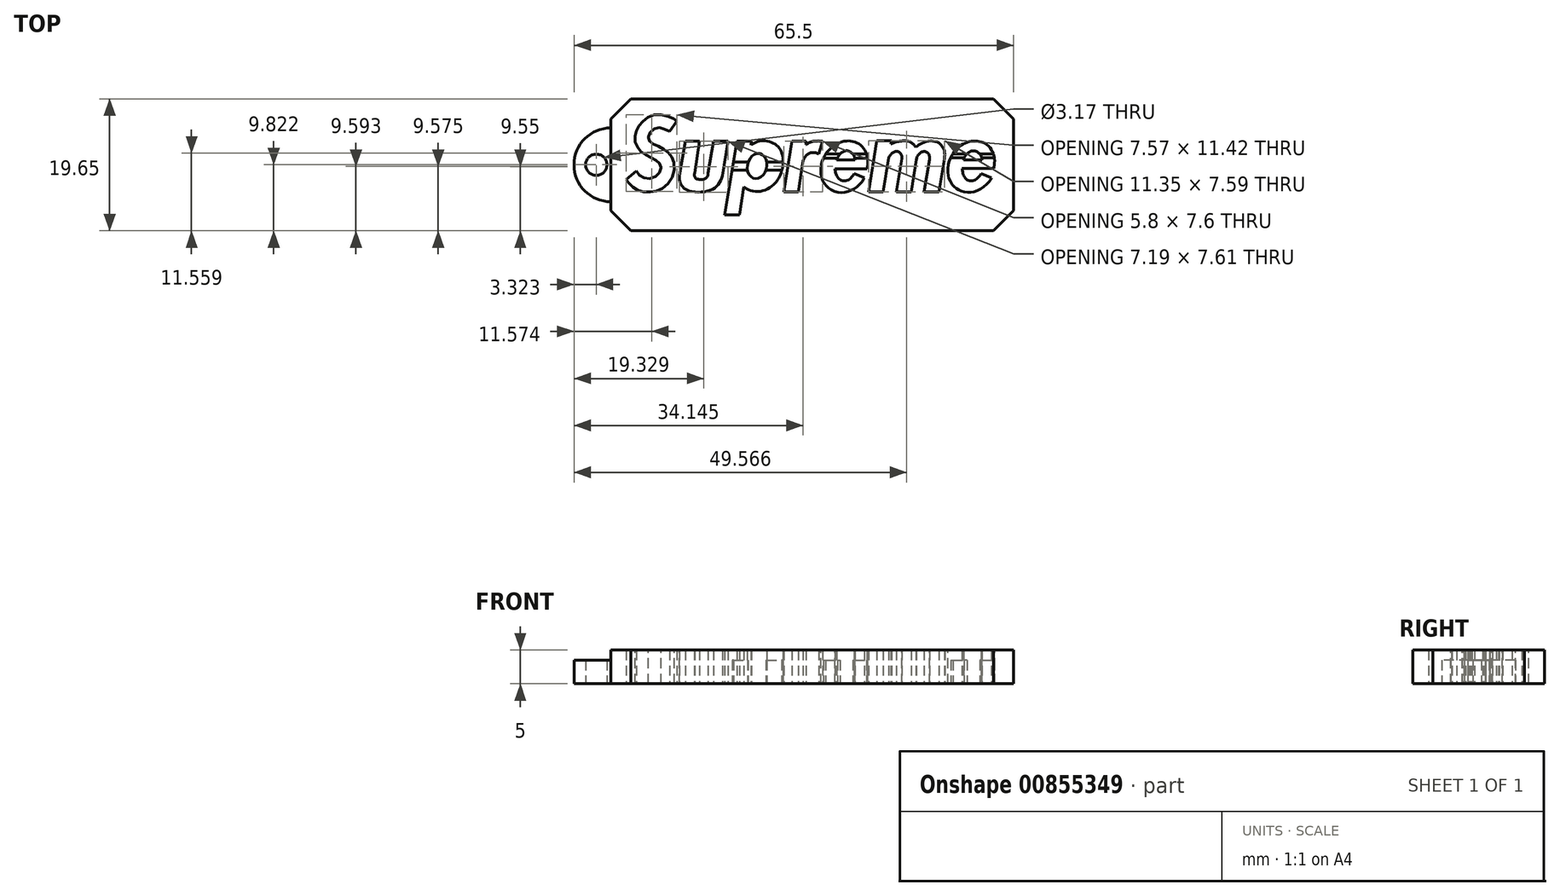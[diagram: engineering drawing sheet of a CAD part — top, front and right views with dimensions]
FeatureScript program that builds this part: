
annotation { "Feature Type Name" : "Feature", "Feature Type Description" : "" }
export const myFeature = defineFeature(function(context is Context, id is Id, definition is map)
    precondition{}
    {
        {
            var Q0;
            Q0=qCreatedBy(makeId("Top.planeOp"),FACE);
            var sketch = newSketch(context, id + "F0", { "sketchPlane" : qUnion([Q0])});
            skLineSegment(sketch, "E0", {"start": v(-20.13, 12.27) * mm, "end": v(-21.24, 10.76) * mm});
            skLineSegment(sketch, "E1", {"start": v(-26.2, 4.84) * mm, "end": v(-27.7, 3.62) * mm});
            skLineSegment(sketch, "E2", {"start": v(-18.91, 9.32) * mm, "end": v(-16.78, 9.32) * mm});
            skLineSegment(sketch, "E3", {"start": v(-18.91, 9.32) * mm, "end": v(-19.76, 4.22) * mm});
            skLineSegment(sketch, "E4", {"start": v(-12.57, 9.32) * mm, "end": v(-13.34, 4.17) * mm});
            skLineSegment(sketch, "E5", {"start": v(-16.78, 9.32) * mm, "end": v(-17.52, 4.58) * mm});
            skLineSegment(sketch, "E6", {"start": v(-14.7, 9.32) * mm, "end": v(-15.5, 4.52) * mm});
            skLineSegment(sketch, "E7", {"start": v(-11.2, 9.31) * mm, "end": v(-9.07, 9.31) * mm});
            skLineSegment(sketch, "E8", {"start": v(-9.07, 9.31) * mm, "end": v(-9.14, 8.73) * mm});
            skLineSegment(sketch, "E9", {"start": v(-11.2, 9.31) * mm, "end": v(-13.03, -1.66) * mm});
            skLineSegment(sketch, "E10", {"start": v(-13.03, -1.66) * mm, "end": v(-10.85, -1.66) * mm});
            skLineSegment(sketch, "E11", {"start": v(-10.85, -1.66) * mm, "end": v(-10.17, 2.52) * mm});
            skLineSegment(sketch, "E12", {"start": v(-3.04, 9.32) * mm, "end": v(-0.9, 9.32) * mm});
            skLineSegment(sketch, "E13", {"start": v(-0.9, 9.32) * mm, "end": v(-0.95, 8.78) * mm});
            skLineSegment(sketch, "E14", {"start": v(-3.04, 9.32) * mm, "end": v(-4.25, 1.75) * mm});
            skLineSegment(sketch, "E15", {"start": v(-4.25, 1.75) * mm, "end": v(-2.07, 1.75) * mm});
            skLineSegment(sketch, "E16", {"start": v(-2.07, 1.75) * mm, "end": v(-1.33, 6.4) * mm});
            skLineSegment(sketch, "E17", {"start": v(3.64, 6.52) * mm, "end": v(6.38, 6.52) * mm});
            skLineSegment(sketch, "E18", {"start": v(3.43, 5.2) * mm, "end": v(8.15, 5.2) * mm});
            skLineSegment(sketch, "E19", {"start": v(6.25, 4.47) * mm, "end": v(7.79, 3.88) * mm});
            skLineSegment(sketch, "E20", {"start": v(9.64, 9.35) * mm, "end": v(8.4, 1.77) * mm});
            skLineSegment(sketch, "E21", {"start": v(8.4, 1.77) * mm, "end": v(10.57, 1.77) * mm});
            skLineSegment(sketch, "E22", {"start": v(18.92, 1.77) * mm, "end": v(19.72, 6.72) * mm});
            skLineSegment(sketch, "E23", {"start": v(9.64, 9.35) * mm, "end": v(11.83, 9.35) * mm});
            skLineSegment(sketch, "E24", {"start": v(11.83, 9.35) * mm, "end": v(11.75, 8.85) * mm});
            skLineSegment(sketch, "E25", {"start": v(13.34, 6.69) * mm, "end": v(12.56, 1.77) * mm});
            skLineSegment(sketch, "E26", {"start": v(15.51, 6.6) * mm, "end": v(14.75, 1.77) * mm});
            skLineSegment(sketch, "E27", {"start": v(17.5, 6.6) * mm, "end": v(16.69, 1.77) * mm});
            skLineSegment(sketch, "E28", {"start": v(22.59, 6.5) * mm, "end": v(25.34, 6.5) * mm});
            skLineSegment(sketch, "E29", {"start": v(22.35, 5.22) * mm, "end": v(27.06, 5.22) * mm});
            skLineSegment(sketch, "E30", {"start": v(25.19, 4.5) * mm, "end": v(26.72, 3.88) * mm});
            skFitSpline(sketch, "E31", {"points": [v(-20.13, 12.27) * mm, v(-20.76, 12.7) * mm, v(-22.11, 13.2) * mm, v(-23.8, 13.15) * mm, v(-25.2, 12.27) * mm, v(-25.93, 11.36) * mm, v(-26.3, 10.37) * mm, v(-26.36, 9.25) * mm, v(-25.87, 8.18) * mm, v(-25.1, 7.42) * mm, v(-23.81, 6.77) * mm, v(-23.11, 6.36) * mm, v(-22.57, 5.74) * mm, v(-22.67, 4.82) * mm, v(-23.38, 4) * mm, v(-24.59, 3.73) * mm, v(-25.6, 4.14) * mm, v(-26.2, 4.84) * mm], "startDerivative": vector(-11.62, 8.81) * mm, "endDerivative": vector(-10.29, 14.16) * mm});
            skFitSpline(sketch, "E32", {"points": [v(-27.7, 3.62) * mm, v(-27.33, 3.07) * mm, v(-26.53, 2.34) * mm, v(-25.49, 1.83) * mm, v(-24.08, 1.73) * mm, v(-22.83, 2) * mm, v(-21.52, 2.96) * mm, v(-20.6, 4.68) * mm, v(-20.7, 6.46) * mm, v(-21.18, 7.32) * mm, v(-21.96, 8.03) * mm, v(-22.95, 8.56) * mm, v(-23.88, 9) * mm, v(-24.3, 9.42) * mm, v(-24.39, 10.06) * mm, v(-23.98, 10.79) * mm, v(-23.08, 11.3) * mm, v(-22.14, 11.16) * mm, v(-21.24, 10.76) * mm], "startDerivative": vector(7.43, -12.37) * mm, "endDerivative": vector(16.77, -8.2) * mm});
            skFitSpline(sketch, "E33", {"points": [v(-19.76, 4.22) * mm, v(-19.76, 3.4) * mm, v(-19.1, 2.3) * mm, v(-17.7, 1.77) * mm, v(-15.88, 1.8) * mm, v(-14.59, 2.32) * mm, v(-13.86, 3.06) * mm, v(-13.34, 4.17) * mm], "startDerivative": vector(-0.86, -6.8) * mm, "endDerivative": vector(3.3, 8.4) * mm});
            skFitSpline(sketch, "E34", {"points": [v(-17.52, 4.58) * mm, v(-17.52, 4.17) * mm, v(-17.35, 3.77) * mm, v(-16.92, 3.62) * mm, v(-16.36, 3.59) * mm, v(-15.88, 3.77) * mm, v(-15.6, 4.1) * mm, v(-15.5, 4.52) * mm], "startDerivative": vector(-0.2, -2.97) * mm, "endDerivative": vector(0.35, 3.22) * mm});
            skLineSegment(sketch, "E35.trimOffspring", {"start": v(-14.7, 9.32) * mm, "end": v(-12.57, 9.32) * mm});
            skEllipse(sketch, "E36", {"center": v(-8.2, 5.6) * mm, "majorRadius": 1.9 * mm, "minorRadius": 1.44 * mm, "majorAxis": v(0.22, 0.98)});
            skFitSpline(sketch, "E37", {"points": [v(-9.14, 8.73) * mm, v(-8.13, 9.26) * mm, v(-6.71, 9.35) * mm, v(-5.34, 8.73) * mm, v(-4.62, 7.79) * mm, v(-4.33, 6.2) * mm, v(-4.76, 4.2) * mm, v(-5.68, 2.9) * mm, v(-7.67, 1.85) * mm, v(-9.7, 2.16) * mm, v(-10.17, 2.52) * mm], "startDerivative": vector(10.84, 6.9) * mm, "endDerivative": vector(-5.7, 5.72) * mm});
            skFitSpline(sketch, "E38", {"points": [v(-0.95, 8.78) * mm, v(0, 9.26) * mm, v(1.56, 9.33) * mm], "startDerivative": vector(1.92, 1.26) * mm, "endDerivative": vector(3.05, -0.12) * mm});
            skLineSegment(sketch, "E39", {"start": v(1.56, 9.33) * mm, "end": v(1, 7.4) * mm});
            skFitSpline(sketch, "E40", {"points": [v(-1.33, 6.4) * mm, v(-0.82, 7.24) * mm, v(0.11, 7.62) * mm, v(1, 7.4) * mm], "startDerivative": vector(1.2, 2.73) * mm, "endDerivative": vector(2.66, -1.05) * mm});
            skFitSpline(sketch, "E41", {"points": [v(3.64, 6.52) * mm, v(4.18, 7.4) * mm, v(5.24, 7.89) * mm, v(6.2, 7.19) * mm, v(6.38, 6.52) * mm], "startDerivative": vector(1.66, 3.64) * mm, "endDerivative": vector(0.33, -3.12) * mm});
            skFitSpline(sketch, "E42", {"points": [v(8.15, 5.2) * mm, v(8.3, 6.03) * mm, v(8.15, 7.13) * mm, v(7.79, 8.05) * mm, v(7.07, 8.82) * mm, v(6.2, 9.24) * mm, v(5.15, 9.34) * mm, v(3.86, 9) * mm, v(2.92, 8.39) * mm, v(2.2, 7.65) * mm, v(1.7, 6.8) * mm, v(1.35, 5.7) * mm, v(1.3, 4.54) * mm, v(1.58, 3.4) * mm, v(2.25, 2.5) * mm, v(3.17, 1.9) * mm, v(4.5, 1.65) * mm, v(5.69, 1.94) * mm, v(6.76, 2.58) * mm, v(7.6, 3.52) * mm, v(7.79, 3.88) * mm], "startDerivative": vector(4.46, 17.79) * mm, "endDerivative": vector(4.42, 10.4) * mm});
            skFitSpline(sketch, "E43", {"points": [v(6.25, 4.47) * mm, v(6.02, 4.1) * mm, v(5.38, 3.54) * mm, v(4.5, 3.4) * mm, v(3.85, 3.88) * mm, v(3.48, 4.6) * mm, v(3.43, 5.2) * mm], "startDerivative": vector(-1.48, -2.67) * mm, "endDerivative": vector(0, 3.83) * mm});
            skFitSpline(sketch, "E44", {"points": [v(11.41, 6.83) * mm, v(11.8, 7.4) * mm, v(12.42, 7.79) * mm, v(13.06, 7.59) * mm, v(13.37, 7.08) * mm, v(13.34, 6.69) * mm], "startDerivative": vector(1.57, 2.8) * mm, "endDerivative": vector(-0.51, -2.35) * mm});
            skFitSpline(sketch, "E45", {"points": [v(15.51, 6.6) * mm, v(15.78, 7.22) * mm, v(16.28, 7.67) * mm, v(16.79, 7.78) * mm, v(17.24, 7.54) * mm, v(17.47, 7.06) * mm, v(17.5, 6.6) * mm], "startDerivative": vector(1.16, 3.5) * mm, "endDerivative": vector(-0.05, -3) * mm});
            skFitSpline(sketch, "E46", {"points": [v(11.75, 8.85) * mm, v(12.3, 9.13) * mm, v(13.4, 9.35) * mm, v(14.5, 9.23) * mm, v(15.14, 8.8) * mm, v(15.43, 8.42) * mm], "startDerivative": vector(2.8, 1.66) * mm, "endDerivative": vector(1.68, -2.39) * mm});
            skFitSpline(sketch, "E47", {"points": [v(15.43, 8.42) * mm, v(16.2, 8.94) * mm, v(17.5, 9.34) * mm, v(18.76, 9.11) * mm, v(19.27, 8.68) * mm, v(19.64, 8.08) * mm, v(19.75, 7.09) * mm, v(19.72, 6.72) * mm], "startDerivative": vector(4.74, 3.64) * mm, "endDerivative": vector(-0.44, -3.35) * mm});
            skLineSegment(sketch, "E48.trimOffspring", {"start": v(11.41, 6.83) * mm, "end": v(10.57, 1.77) * mm});
            skLineSegment(sketch, "E49.trimOffspring", {"start": v(12.56, 1.77) * mm, "end": v(14.75, 1.77) * mm});
            skLineSegment(sketch, "E50.trimOffspring", {"start": v(16.69, 1.77) * mm, "end": v(18.92, 1.77) * mm});
            skFitSpline(sketch, "E51", {"points": [v(25.34, 6.5) * mm, v(25.05, 7.33) * mm, v(24.18, 7.86) * mm, v(23.34, 7.65) * mm, v(22.7, 6.95) * mm, v(22.59, 6.5) * mm], "startDerivative": vector(-0.77, 4.25) * mm, "endDerivative": vector(-0.26, -2.86) * mm});
            skFitSpline(sketch, "E52", {"points": [v(27.06, 5.22) * mm, v(27.17, 6.07) * mm, v(27.11, 7.06) * mm, v(26.68, 8.06) * mm, v(26.01, 8.82) * mm, v(25.16, 9.21) * mm, v(24.45, 9.33) * mm, v(23.59, 9.28) * mm, v(22.59, 8.94) * mm, v(21.67, 8.28) * mm, v(21.02, 7.5) * mm, v(20.52, 6.58) * mm, v(20.24, 5.51) * mm, v(20.24, 4.36) * mm, v(20.42, 3.7) * mm, v(20.93, 2.78) * mm, v(21.37, 2.35) * mm, v(21.86, 2.03) * mm, v(22.47, 1.77) * mm, v(23.45, 1.69) * mm, v(24.27, 1.83) * mm, v(25.28, 2.3) * mm, v(26.15, 3.04) * mm, v(26.66, 3.65) * mm, v(26.72, 3.88) * mm], "startDerivative": vector(3.51, 20.16) * mm, "endDerivative": vector(1.13, 9.7) * mm});
            skFitSpline(sketch, "E53", {"points": [v(25.19, 4.5) * mm, v(25.01, 4.22) * mm, v(24.56, 3.75) * mm, v(24.01, 3.46) * mm, v(23.35, 3.45) * mm, v(22.87, 3.75) * mm, v(22.59, 4.22) * mm, v(22.39, 4.9) * mm, v(22.35, 5.22) * mm], "startDerivative": vector(-1.5, -2.65) * mm, "endDerivative": vector(-0.25, 3) * mm});
            skLineSegment(sketch, "E54.bottom", {"start": v(-29.99, 15.62) * mm, "end": v(30.01, 15.62) * mm});
            skLineSegment(sketch, "E54.top", {"start": v(-29.99, -4.03) * mm, "end": v(30.01, -4.03) * mm});
            skLineSegment(sketch, "E54.left", {"start": v(-29.99, 15.62) * mm, "end": v(-29.99, -4.03) * mm});
            skLineSegment(sketch, "E54.right", {"start": v(30.01, 15.62) * mm, "end": v(30.01, -4.03) * mm});
            skArc(sketch, "E55", {"start": v(-29.99, 11.3) * mm, "mid": v(-35.49, 5.8) * mm, "end": v(-29.99, 0.3) * mm});
            skCircle(sketch, "E56", {"center": v(-32.17, 5.8) * mm, "radius": 1.59 * mm});
            skLineSegment(sketch, "E57.bottom", {"start": v(-11.93, 4.97) * mm, "end": v(-9.63, 4.97) * mm});
            skLineSegment(sketch, "E57.top", {"start": v(-11.72, 6.2) * mm, "end": v(-9.53, 6.2) * mm});
            skLineSegment(sketch, "E58.trimOffspring", {"start": v(-6.77, 6.2) * mm, "end": v(-4.33, 6.2) * mm});
            skLineSegment(sketch, "E59.trimOffspring", {"start": v(-6.89, 4.97) * mm, "end": v(-4.5, 4.97) * mm});
            skLineSegment(sketch, "E60.bottom", {"start": v(1.7, 6.8) * mm, "end": v(3.77, 6.8) * mm});
            skLineSegment(sketch, "E60.top", {"start": v(2.03, 7.4) * mm, "end": v(4.18, 7.4) * mm});
            skLineSegment(sketch, "E61.bottom", {"start": v(20.64, 6.87) * mm, "end": v(22.66, 6.87) * mm});
            skLineSegment(sketch, "E61.top", {"start": v(20.97, 7.43) * mm, "end": v(23.07, 7.43) * mm});
            skPoint(sketch, "E62.orphan", {"position": v(8.45, 7.4) * mm});
            skLineSegment(sketch, "E63.trimOffspring", {"start": v(6.04, 7.4) * mm, "end": v(8.07, 7.4) * mm});
            skLineSegment(sketch, "E64.trimOffspring", {"start": v(6.35, 6.8) * mm, "end": v(8.22, 6.8) * mm});
            skLineSegment(sketch, "E65.trimOffspring", {"start": v(25.26, 6.87) * mm, "end": v(27.15, 6.87) * mm});
            skLineSegment(sketch, "E66.trimOffspring", {"start": v(24.97, 7.43) * mm, "end": v(27, 7.43) * mm});
            skSolve(sketch);
        }
        {
            var Q0;
            Q0=makeQuery(id+"F0.imprint","IMPRINT",FACE,{"disambiguationData":[TD([[makeQuery(id+"F0.imprint","IMPRINT",EDGE,{"derivedFrom":sQuery(id+"F0.wireOp",EDGE,"E0")}),1.0]])]});
            var Q1;
            Q1=makeQuery(id+"F0.imprint","IMPRINT",FACE,{"disambiguationData":[TD([[makeQuery(id+"F0.imprint","IMPRINT",EDGE,{"derivedFrom":sQuery(id+"F0.wireOp",EDGE,"E36")}),1.0]])]});
            var Q2;
            Q2=makeQuery(id+"F0.imprint","IMPRINT",FACE,{"disambiguationData":[TD([[makeQuery(id+"F0.imprint","IMPRINT",EDGE,{"derivedFrom":sQuery(id+"F0.wireOp",EDGE,"E17")}),1.0]])]});
            var Q3;
            Q3=makeQuery(id+"F0.imprint","IMPRINT",FACE,{"disambiguationData":[TD([[makeQuery(id+"F0.imprint","IMPRINT",EDGE,{"derivedFrom":sQuery(id+"F0.wireOp",EDGE,"E28")}),1.0]])]});
            extrude(context, id + "F1", {"entities" : qUnion([Q0, Q1, Q2, Q3]), "depth" : 5 * mm, "offsetDistance" : 25 * mm});
        }
        {
            var Q0;
            {var subQ0=sQuery(id+"F0.wireOp",EDGE,"E55");Q0=makeQuery(id+"F0.imprint","IMPRINT",FACE,{"disambiguationData":[TD([[makeQuery(id+"F0.imprint","IMPRINT",EDGE,{"derivedFrom":subQ0}),1.0]])]});}
            var Q1;
            {var subQ0=sQuery(id+"F0.wireOp",EDGE,"E57.bottom");Q1=makeQuery(id+"F0.imprint","IMPRINT",FACE,{"disambiguationData":[TD([[makeQuery(id+"F0.imprint","IMPRINT",EDGE,{"derivedFrom":subQ0}),1.0]])]});}
            var Q2;
            {var subQ0=sQuery(id+"F0.wireOp",EDGE,"E58.trimOffspring");Q2=makeQuery(id+"F0.imprint","IMPRINT",FACE,{"disambiguationData":[TD([[makeQuery(id+"F0.imprint","IMPRINT",EDGE,{"derivedFrom":subQ0}),-1.0]])]});}
            var Q3;
            {var subQ0=sQuery(id+"F0.wireOp",EDGE,"E60.bottom");Q3=makeQuery(id+"F0.imprint","IMPRINT",FACE,{"disambiguationData":[TD([[makeQuery(id+"F0.imprint","IMPRINT",EDGE,{"derivedFrom":subQ0}),1.0]])]});}
            var Q4;
            {var subQ0=sQuery(id+"F0.wireOp",EDGE,"E63.trimOffspring");Q4=makeQuery(id+"F0.imprint","IMPRINT",FACE,{"disambiguationData":[TD([[makeQuery(id+"F0.imprint","IMPRINT",EDGE,{"derivedFrom":subQ0}),-1.0]])]});}
            var Q5;
            {var subQ0=sQuery(id+"F0.wireOp",EDGE,"E61.bottom");Q5=makeQuery(id+"F0.imprint","IMPRINT",FACE,{"disambiguationData":[TD([[makeQuery(id+"F0.imprint","IMPRINT",EDGE,{"derivedFrom":subQ0}),1.0]])]});}
            var Q6;
            {var subQ0=sQuery(id+"F0.wireOp",EDGE,"E65.trimOffspring");Q6=makeQuery(id+"F0.imprint","IMPRINT",FACE,{"disambiguationData":[TD([[makeQuery(id+"F0.imprint","IMPRINT",EDGE,{"derivedFrom":subQ0}),1.0]])]});}
            extrude(context, id + "F2", {"entities" : qUnion([Q0, Q1, Q2, Q3, Q4, Q5, Q6]), "operationType" : NewBodyOperationType.ADD, "depth" : 3.5 * mm, "offsetDistance" : 25 * mm});
        }
        {
            var Q0;
            Q0=makeQuery(id+"F1.opExtrude","SWEPT_EDGE",EDGE,{"disambiguationData":[OSD([sQuery(id+"F0.wireOp",EDGE,"E54.top"),sQuery(id+"F0.wireOp",EDGE,"E54.left")])]});
            var Q1;
            Q1=makeQuery(id+"F1.opExtrude","SWEPT_EDGE",EDGE,{"disambiguationData":[OSD([sQuery(id+"F0.wireOp",EDGE,"E54.top"),sQuery(id+"F0.wireOp",EDGE,"E54.right")])]});
            var Q2;
            Q2=makeQuery(id+"F1.opExtrude","SWEPT_EDGE",EDGE,{"disambiguationData":[OSD([sQuery(id+"F0.wireOp",EDGE,"E54.bottom"),sQuery(id+"F0.wireOp",EDGE,"E54.right")])]});
            var Q3;
            Q3=makeQuery(id+"F1.opExtrude","SWEPT_EDGE",EDGE,{"disambiguationData":[OSD([sQuery(id+"F0.wireOp",EDGE,"E54.bottom"),sQuery(id+"F0.wireOp",EDGE,"E54.left")])]});
            chamfer(context, id + "F3", {"entities" : qUnion([Q0, Q1, Q2, Q3]), "width" : 3 * mm, "tangentPropagation" : true});
        }
    });
